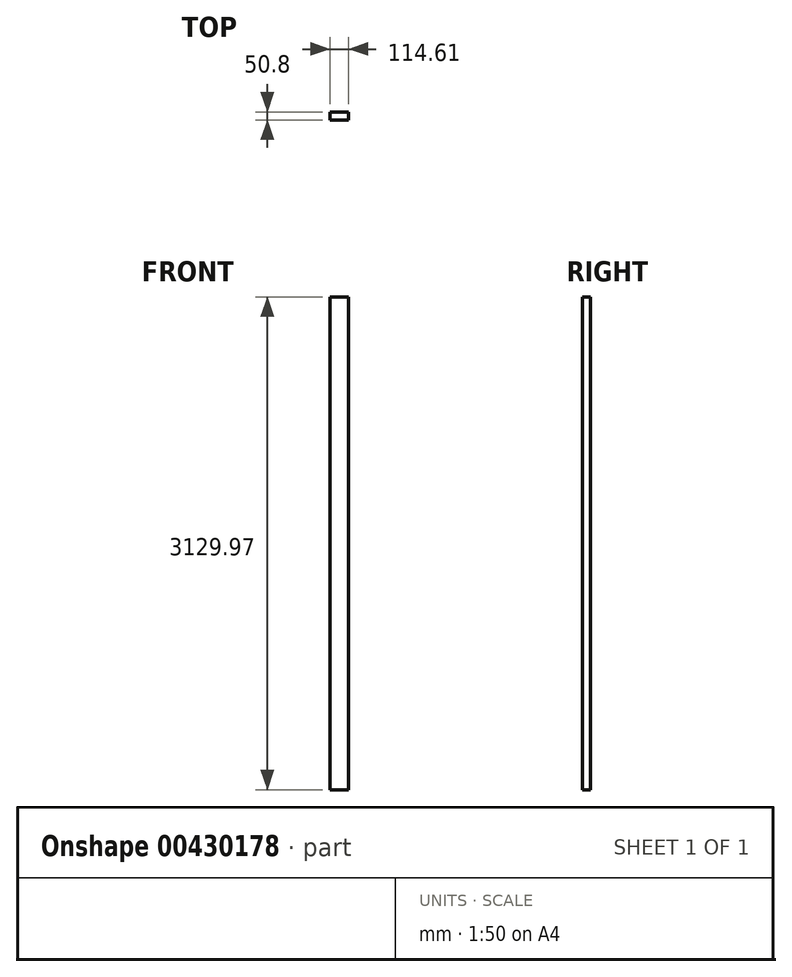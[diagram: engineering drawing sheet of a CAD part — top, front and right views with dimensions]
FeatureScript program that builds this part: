
annotation { "Feature Type Name" : "Feature", "Feature Type Description" : "" }
export const myFeature = defineFeature(function(context is Context, id is Id, definition is map)
    precondition{}
    {
        {
            var Q0;
            Q0=qCreatedBy(makeId("Front.planeOp"),FACE);
            var sketch = newSketch(context, id + "F0", { "sketchPlane" : qUnion([Q0])});
            skLineSegment(sketch, "E0.bottom", {"start": v(-27.76, 19.36) * mm, "end": v(-14.75, 19.36) * mm});
            skLineSegment(sketch, "E0.top", {"start": v(-27.76, -62.61) * mm, "end": v(-14.75, -62.61) * mm});
            skLineSegment(sketch, "E0.left", {"start": v(-27.76, 19.36) * mm, "end": v(-27.76, -62.61) * mm});
            skLineSegment(sketch, "E0.right", {"start": v(-14.75, 19.36) * mm, "end": v(-14.75, -62.61) * mm});
            skSolve(sketch);
        }
        {
            var Q0;
            Q0=makeQuery(id+"F0.imprint","IMPRINT",FACE,{"disambiguationData":[TD([[makeQuery(id+"F0.imprint","IMPRINT",EDGE,{"derivedFrom":sQuery(id+"F0.wireOp",EDGE,"E0.bottom")}),-1.0]])]});
            extrude(context, id + "F1", {"entities" : qUnion([Q0]), "depth" : 50.8 * mm});
        }
        {
            var Q0;
            Q0=makeQuery(id+"F1.opExtrude","SWEPT_FACE",FACE,{"disambiguationData":[OSD([sQuery(id+"F0.wireOp",EDGE,"E0.right")])]});
            extrude(context, id + "F2", {"entities" : qUnion([Q0]), "operationType" : NewBodyOperationType.ADD, "depth" : 101.6 * mm});
        }
        {
            var Q0;
            {var subQ0=sQuery(id+"F0.wireOp",EDGE,"E0.bottom");Q0=makeQuery(id+"F2.boolean.opBoolean","MERGE",FACE,{"derivedFrom":[makeQuery(id+"F1.opExtrude","SWEPT_FACE",FACE,{"disambiguationData":[OSD([subQ0])]}),makeQuery(id+"F2.opExtrude","SWEPT_FACE",FACE,{"disambiguationData":[OSD([subQ0,sQuery(id+"F0.wireOp",EDGE,"E0.right")])]})]});}
            extrude(context, id + "F3", {"entities" : qUnion([Q0]), "operationType" : NewBodyOperationType.ADD, "depth" : 3048 * mm});
        }
    });
